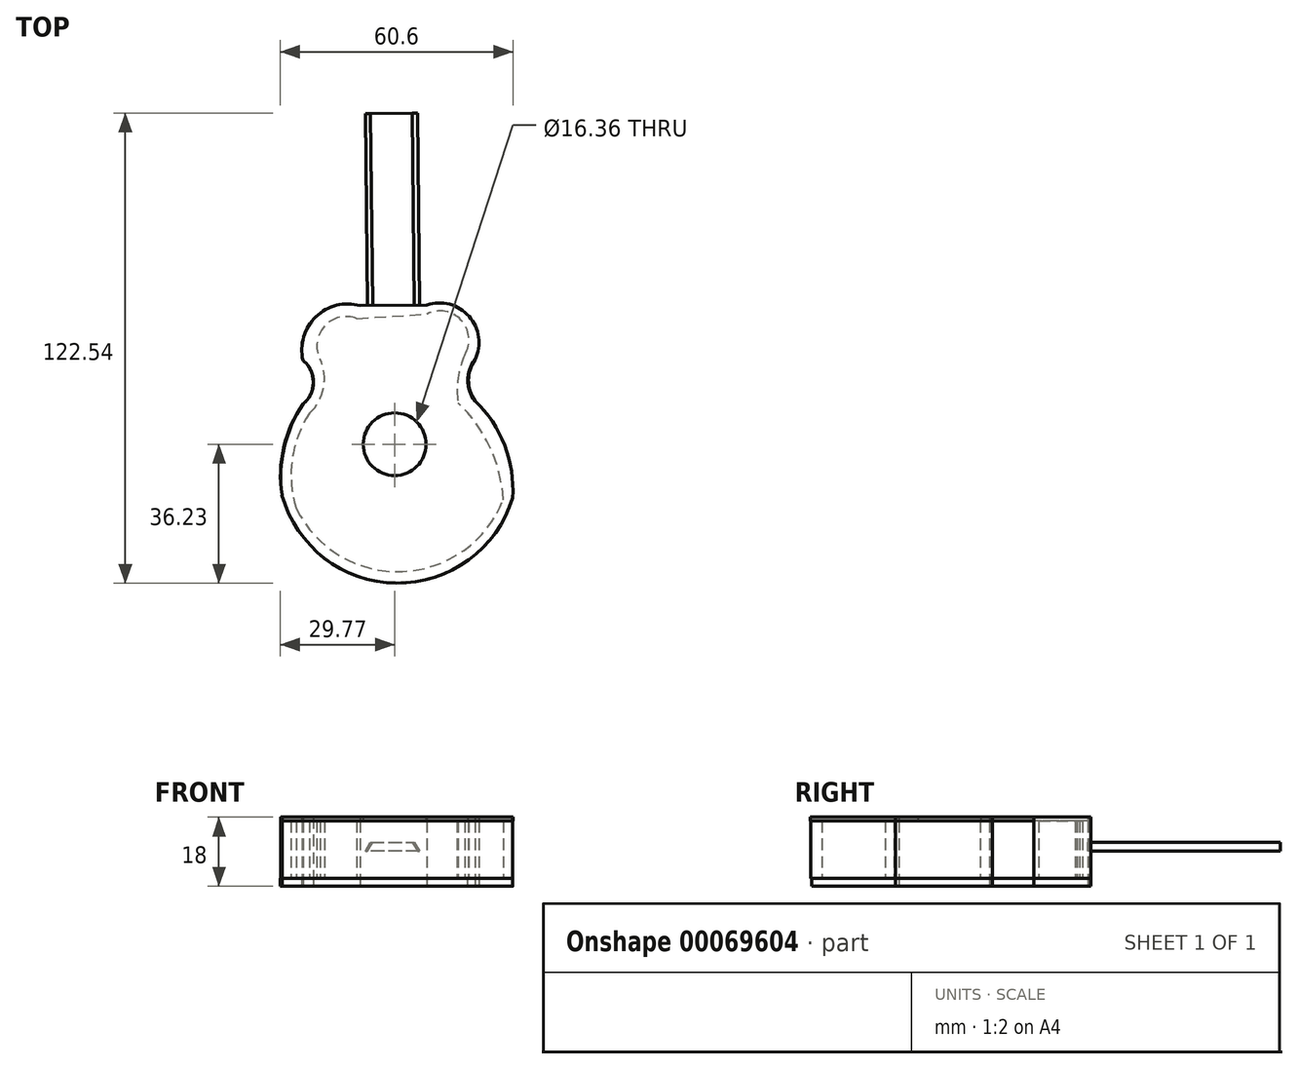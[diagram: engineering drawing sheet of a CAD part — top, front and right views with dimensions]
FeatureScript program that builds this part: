
annotation { "Feature Type Name" : "Feature", "Feature Type Description" : "" }
export const myFeature = defineFeature(function(context is Context, id is Id, definition is map)
    precondition{}
    {
        {
            var Q0;
            Q0=qCreatedBy(makeId("Top.planeOp"),FACE);
            var sketch = newSketch(context, id + "F0", { "sketchPlane" : qUnion([Q0])});
            skArc(sketch, "E0", {"start": v(-29.38, -31.63) * mm, "mid": v(0.4, -54.35) * mm, "end": v(30.75, -32.42) * mm});
            skArc(sketch, "E1", {"start": v(30.75, -32.42) * mm, "mid": v(28.56, -18.73) * mm, "end": v(20.96, -7.15) * mm});
            skArc(sketch, "E2", {"start": v(-23.9, -7.93) * mm, "mid": v(-28.94, -19.25) * mm, "end": v(-29.38, -31.63) * mm});
            skArc(sketch, "E3", {"start": v(20.96, 3.62) * mm, "mid": v(18.98, -1.76) * mm, "end": v(20.96, -7.15) * mm});
            skArc(sketch, "E4", {"start": v(-23.9, -7.93) * mm, "mid": v(-21.22, -2.25) * mm, "end": v(-23.9, 3.43) * mm});
            skArc(sketch, "E5", {"start": v(20.96, 3.62) * mm, "mid": v(19.4, 14.9) * mm, "end": v(8.42, 17.92) * mm});
            skArc(sketch, "E6", {"start": v(-9, 17.73) * mm, "mid": v(-20.52, 14.8) * mm, "end": v(-23.9, 3.43) * mm});
            skLineSegment(sketch, "E7", {"start": v(-9, 17.73) * mm, "end": v(8.42, 17.92) * mm});
            skSolve(sketch);
        }
        {
            var Q0;
            Q0 = qSketchRegion(id + "F0", true);
            extrude(context, id + "F1", {"entities" : qUnion([Q0]), "depth" : 2 * mm});
        }
        {
            var Q0;
            Q0=makeQuery(id+"F1.opExtrude","CAP_FACE",FACE,{"disambiguationData":[OSD([sQuery(id+"F0.wireOp",EDGE,"E0"),sQuery(id+"F0.wireOp",EDGE,"E1"),sQuery(id+"F0.wireOp",EDGE,"E2"),sQuery(id+"F0.wireOp",EDGE,"E3"),sQuery(id+"F0.wireOp",EDGE,"E4"),sQuery(id+"F0.wireOp",EDGE,"E5"),sQuery(id+"F0.wireOp",EDGE,"E6"),sQuery(id+"F0.wireOp",EDGE,"E7")])],"isStart":false});
            var sketch = newSketch(context, id + "F2", { "sketchPlane" : qUnion([Q0])});
            skArc(sketch, "E8", {"start": v(-9, 17.73) * mm, "mid": v(-20.34, 14.62) * mm, "end": v(-23.9, 3.43) * mm});
            skArc(sketch, "E9", {"start": v(-23.9, -7.93) * mm, "mid": v(-21.16, -2.25) * mm, "end": v(-23.9, 3.43) * mm});
            skArc(sketch, "E10", {"start": v(-23.9, -7.93) * mm, "mid": v(-28.9, -19.26) * mm, "end": v(-29.38, -31.63) * mm});
            skArc(sketch, "E11", {"start": v(-29.38, -31.63) * mm, "mid": v(0.4, -54.6) * mm, "end": v(30.75, -32.42) * mm});
            skArc(sketch, "E12", {"start": v(30.75, -32.42) * mm, "mid": v(28.53, -18.74) * mm, "end": v(20.96, -7.15) * mm});
            skArc(sketch, "E13", {"start": v(20.96, 3.62) * mm, "mid": v(19.24, -1.76) * mm, "end": v(20.96, -7.15) * mm});
            skArc(sketch, "E14", {"start": v(20.96, 3.62) * mm, "mid": v(19.4, 14.9) * mm, "end": v(8.42, 17.92) * mm});
            skArc(sketch, "E15", {"start": v(18.31, 4.92) * mm, "mid": v(17.36, 13.94) * mm, "end": v(8.42, 15.52) * mm});
            skArc(sketch, "E16", {"start": v(18.31, 4.92) * mm, "mid": v(16.5, -1.22) * mm, "end": v(16.58, -7.61) * mm});
            skArc(sketch, "E17", {"start": v(28.34, -32.87) * mm, "mid": v(24.84, -19.13) * mm, "end": v(16.58, -7.61) * mm});
            skArc(sketch, "E18", {"start": v(-25.64, -35.18) * mm, "mid": v(2.1, -51.62) * mm, "end": v(28.34, -32.87) * mm});
            skArc(sketch, "E19", {"start": v(-22.17, -10.31) * mm, "mid": v(-26.72, -22.36) * mm, "end": v(-25.64, -35.18) * mm});
            skArc(sketch, "E20", {"start": v(-22.17, -10.31) * mm, "mid": v(-18.52, -3.72) * mm, "end": v(-19.47, 3.76) * mm});
            skArc(sketch, "E21", {"start": v(-9.83, 14.36) * mm, "mid": v(-18.28, 12.36) * mm, "end": v(-19.47, 3.76) * mm});
            skLineSegment(sketch, "E22", {"start": v(-9.83, 14.36) * mm, "end": v(8.42, 15.52) * mm});
            skLineSegment(sketch, "E23", {"start": v(8.42, 17.92) * mm, "end": v(-9, 17.73) * mm});
            skSolve(sketch);
        }
        {
            var Q0;
            Q0 = qSketchRegion(id + "F2", true);
            extrude(context, id + "F3", {"entities" : qUnion([Q0]), "operationType" : NewBodyOperationType.ADD, "depth" : 15 * mm});
        }
        {
            var Q0;
            Q0=makeQuery(id+"F3.opExtrude","CAP_FACE",FACE,{"disambiguationData":[OSD([sQuery(id+"F2.wireOp",EDGE,"E8"),sQuery(id+"F2.wireOp",EDGE,"E9"),sQuery(id+"F2.wireOp",EDGE,"E10"),sQuery(id+"F2.wireOp",EDGE,"E11"),sQuery(id+"F2.wireOp",EDGE,"E12"),sQuery(id+"F2.wireOp",EDGE,"E13"),sQuery(id+"F2.wireOp",EDGE,"E14"),sQuery(id+"F2.wireOp",EDGE,"E15"),sQuery(id+"F2.wireOp",EDGE,"E16"),sQuery(id+"F2.wireOp",EDGE,"E17"),sQuery(id+"F2.wireOp",EDGE,"E18"),sQuery(id+"F2.wireOp",EDGE,"E19"),sQuery(id+"F2.wireOp",EDGE,"E20"),sQuery(id+"F2.wireOp",EDGE,"E21"),sQuery(id+"F2.wireOp",EDGE,"E22"),sQuery(id+"F2.wireOp",EDGE,"E23")])],"isStart":false});
            var sketch = newSketch(context, id + "F4", { "sketchPlane" : qUnion([Q0])});
            skArc(sketch, "E24", {"start": v(-9, 17.73) * mm, "mid": v(-20.53, 14.83) * mm, "end": v(-23.9, 3.43) * mm});
            skArc(sketch, "E25", {"start": v(-23.9, -7.93) * mm, "mid": v(-21.16, -2.25) * mm, "end": v(-23.9, 3.43) * mm});
            skArc(sketch, "E26", {"start": v(-23.9, -7.93) * mm, "mid": v(-28.8, -19.28) * mm, "end": v(-29.38, -31.63) * mm});
            skArc(sketch, "E27", {"start": v(-29.38, -31.63) * mm, "mid": v(0.4, -54.64) * mm, "end": v(30.75, -32.42) * mm});
            skArc(sketch, "E28", {"start": v(30.75, -32.42) * mm, "mid": v(28.68, -18.69) * mm, "end": v(20.96, -7.15) * mm});
            skArc(sketch, "E29", {"start": v(20.96, 3.62) * mm, "mid": v(19.08, -1.76) * mm, "end": v(20.96, -7.15) * mm});
            skArc(sketch, "E30", {"start": v(20.96, 3.62) * mm, "mid": v(19.4, 14.9) * mm, "end": v(8.42, 17.92) * mm});
            skPoint(sketch, "E31.center.orphan", {"position": v(0, -18.41) * mm});
            skCircle(sketch, "E32", {"center": v(0, -18.41) * mm, "radius": 8.18 * mm});
            skLineSegment(sketch, "E33", {"start": v(-9, 17.73) * mm, "end": v(8.42, 17.92) * mm});
            skSolve(sketch);
        }
        {
            var Q0;
            Q0 = qSketchRegion(id + "F4", true);
            extrude(context, id + "F5", {"entities" : qUnion([Q0]), "operationType" : NewBodyOperationType.ADD, "depth" : 1 * mm});
        }
        {
            var Q0;
            Q0=makeQuery(id+"F5.boolean.opBoolean","MERGE",FACE,{"derivedFrom":[makeQuery(id+"F3.boolean.opBoolean","MERGE",FACE,{"derivedFrom":[makeQuery(id+"F1.opExtrude","SWEPT_FACE",FACE,{"disambiguationData":[OSD([sQuery(id+"F0.wireOp",EDGE,"E7")])]}),makeQuery(id+"F3.opExtrude","SWEPT_FACE",FACE,{"disambiguationData":[OSD([sQuery(id+"F2.wireOp",EDGE,"E23")])]})]}),makeQuery(id+"F5.opExtrude","SWEPT_FACE",FACE,{"disambiguationData":[OSD([sQuery(id+"F4.wireOp",EDGE,"E33")])]})]});
            var sketch = newSketch(context, id + "F6", { "sketchPlane" : qUnion([Q0])});
            skLineSegment(sketch, "E34", {"start": v(5.51, 11.47) * mm, "end": v(-5.36, 11.47) * mm});
            skLineSegment(sketch, "E35", {"start": v(-5.36, 11.47) * mm, "end": v(-6.73, 9.1) * mm});
            skLineSegment(sketch, "E36", {"start": v(-6.73, 9.1) * mm, "end": v(6.83, 9.1) * mm});
            skLineSegment(sketch, "E37", {"start": v(6.83, 9.1) * mm, "end": v(5.51, 11.47) * mm});
            skSolve(sketch);
        }
        {
            var Q0;
            Q0 = qSketchRegion(id + "F6", true);
            extrude(context, id + "F7", {"entities" : qUnion([Q0]), "operationType" : NewBodyOperationType.ADD, "depth" : 50 * mm});
        }
    });
